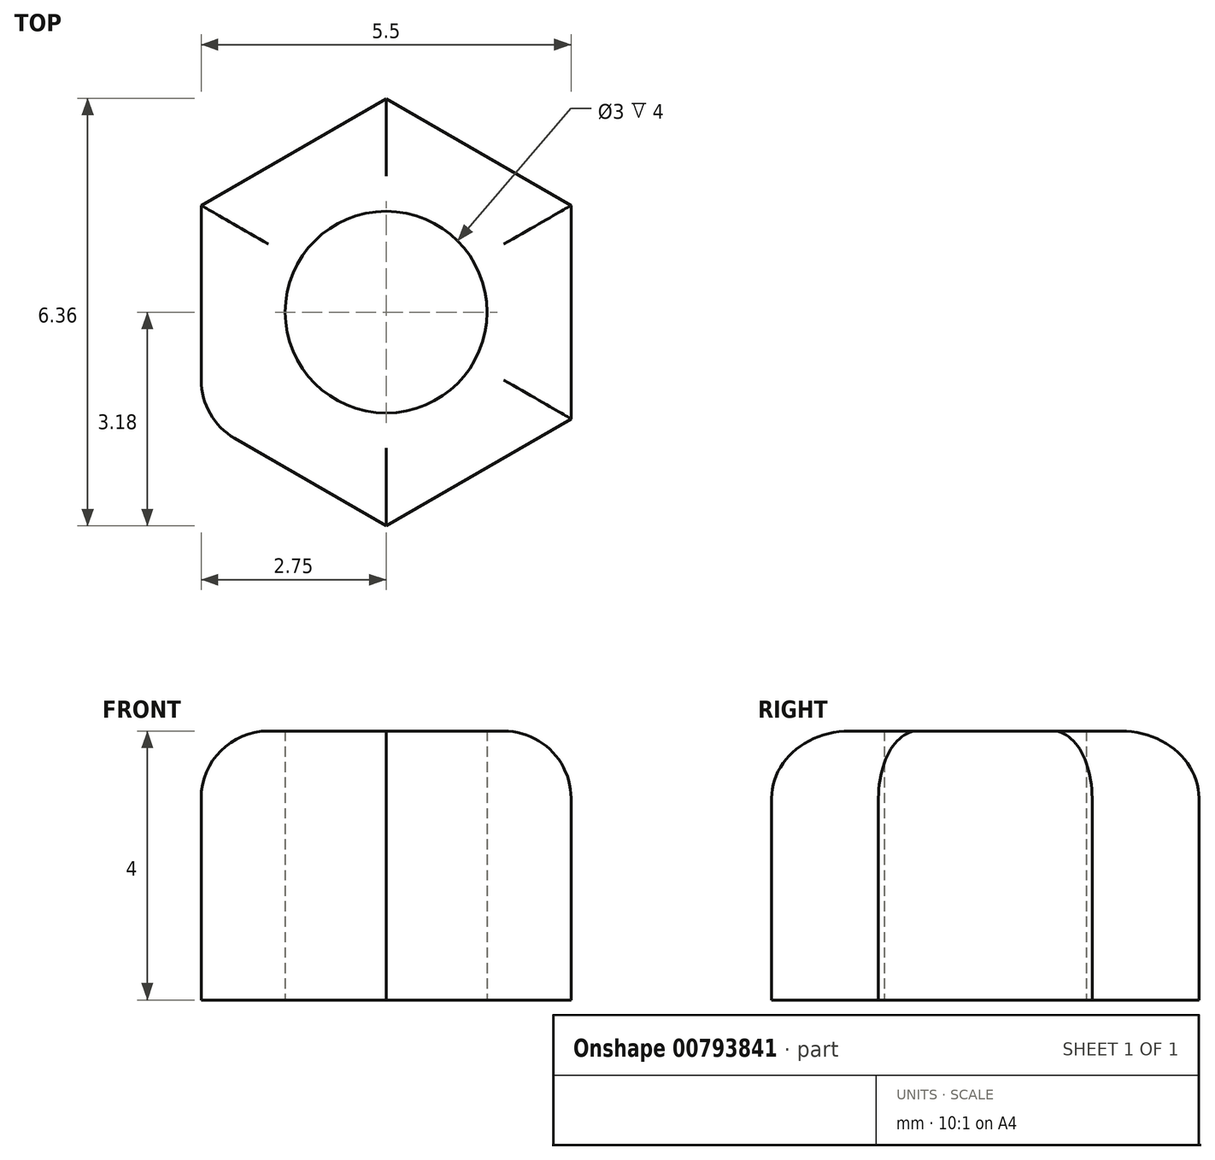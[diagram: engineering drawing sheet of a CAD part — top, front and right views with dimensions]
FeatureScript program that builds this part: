
annotation { "Feature Type Name" : "Feature", "Feature Type Description" : "" }
export const myFeature = defineFeature(function(context is Context, id is Id, definition is map)
    precondition{}
    {
        {
            var Q0;
            Q0=qCreatedBy(makeId("Top.planeOp"),FACE);
            var sketch = newSketch(context, id + "F0", { "sketchPlane" : qUnion([Q0])});
            skCircle(sketch, "E0.cCircle", {"center": v(0, 0) * mm, "radius": 2.75 * mm, "construction": true});
            skLineSegment(sketch, "E0.0", {"start": v(2.75, 1.59) * mm, "end": v(2.75, -1.59) * mm});
            skLineSegment(sketch, "E0.1", {"start": v(2.75, -1.59) * mm, "end": v(0, -3.18) * mm});
            skLineSegment(sketch, "E0.2", {"start": v(0, -3.18) * mm, "end": v(-2.75, -1.59) * mm});
            skLineSegment(sketch, "E0.3", {"start": v(-2.75, -1.59) * mm, "end": v(-2.75, 1.59) * mm});
            skLineSegment(sketch, "E0.4", {"start": v(-2.75, 1.59) * mm, "end": v(0, 3.18) * mm});
            skLineSegment(sketch, "E0.5", {"start": v(0, 3.18) * mm, "end": v(2.75, 1.59) * mm});
            skPoint(sketch, "E0.0.midPoint", {"position": v(2.75, 0) * mm});
            skCircle(sketch, "E1", {"center": v(0, 0) * mm, "radius": 1.5 * mm});
            skSolve(sketch);
        }
        {
            var Q0;
            Q0=qSketchRegion(id+"F0",true);
            extrude(context, id + "F1", {"entities" : qUnion([Q0]), "depth" : 4 * mm, "offsetDistance" : 25 * mm});
        }
        {
            var Q0;
            Q0=makeQuery(id+"F1.opExtrude","CAP_EDGE",EDGE,{"disambiguationData":[OSD([sQuery(id+"F0.wireOp",EDGE,"E0.5")])],"isStart":false});
            var Q1;
            Q1=makeQuery(id+"F1.opExtrude","CAP_EDGE",EDGE,{"disambiguationData":[OSD([sQuery(id+"F0.wireOp",EDGE,"E0.1")])],"isStart":false});
            var Q2;
            Q2=makeQuery(id+"F1.opExtrude","SWEPT_EDGE",EDGE,{"disambiguationData":[OSD([sQuery(id+"F0.wireOp",EDGE,"E0.2"),sQuery(id+"F0.wireOp",EDGE,"E0.3")])]});
            var Q3;
            Q3=makeQuery(id+"F1.opExtrude","CAP_EDGE",EDGE,{"disambiguationData":[OSD([sQuery(id+"F0.wireOp",EDGE,"E0.3")])],"isStart":false});
            var Q4;
            Q4=makeQuery(id+"F1.opExtrude","CAP_EDGE",EDGE,{"disambiguationData":[OSD([sQuery(id+"F0.wireOp",EDGE,"E0.4")])],"isStart":false});
            var Q5;
            Q5=makeQuery(id+"F1.opExtrude","CAP_EDGE",EDGE,{"disambiguationData":[OSD([sQuery(id+"F0.wireOp",EDGE,"E0.0")])],"isStart":false});
            var Q6;
            Q6=makeQuery(id+"F1.opExtrude","CAP_EDGE",EDGE,{"disambiguationData":[OSD([sQuery(id+"F0.wireOp",EDGE,"E0.2")])],"isStart":false});
            fillet(context, id + "F2", {"entities" : qUnion([Q0, Q1, Q2, Q3, Q4, Q5, Q6]), "radius" : 1 * mm, "tangentPropagation" : true, "allowEdgeOverflow" : false});
        }
    });
